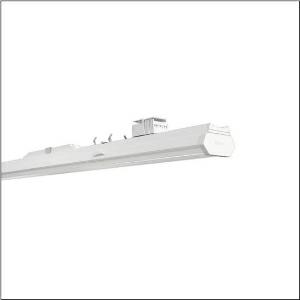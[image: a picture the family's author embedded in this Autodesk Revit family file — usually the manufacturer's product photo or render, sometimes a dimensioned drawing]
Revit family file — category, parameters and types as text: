
# Revit family: licross_r__21_protected_mo_52tp12mn4a5g_3eb5
name_source: partatom
category: Lighting Fixtures
units: mm (PartAtom-declared; Revit-internal decimal feet)

## family parameters
Cut with Voids When Loaded = No
Host = Face
Light Source = No
Part Type = Normal
Room Calculation Point = No
Round Connector Dimension = Use Diameter
Shared = No

## types (1)
- --- (1 x LED, 10750 lm, 60.5 W, 4000K)
    Apparent Load = 61 VA
    CIE Flux Codes = 73 92 98 99 100
    Color Rendering = 80
    Color Temperature = 4000K
    Default Elevation = 1800 mm
    Description = Licross® 21 Protected MO, luminaire insert, of sheet steel, galvanised, coil coated, white, length: 1.500mm, width: 90mm, height: 101mm, LED rated luminous flux: 10.750lm, light colour: 840, control gear: ON/OFF Multilumen, with plug, 3-pole, with phase selection, mains connection: 220..240V, AC, 50/60Hz, rated input power: 61W, halogen-free wiring, primary light control with lens, of plastic, primary optical cover: cover, of PMMA, light emission: direct distribution, primary light characteristic: symmetric, protection rating (complete): IP64, insulation class (complete): insulation class I (protective earthing), certification: CE, ENEC, VDE, UKCA, protection symbol: D if used in an environment with conductive dust loads with corresponding accessories, impact resistance: IK06, permissible ambient temperature for indoor applications: -35..+45°C, corresponds to IFS (International Featured Standards) requirements for safety and quality in the food industry, reducing of maximum allowable ambient temperature of 5°C with ceiling mounting, LABS conformity tested according to VDMA 24364:2018-05, packaging unit: 1 piece
    Height = 92 mm
    Lamp = 1 x LED
    Lamp Light Flux = 10750 lm
    Lamp Power = 60.5 W
    Lamp count = 1
    Length = 1500 mm
    Luminous efficacy = 178 lm/W
    Manufacturer = Siteco
    ModVariant = No
    Model = 52TP12MN4A5G
    Mounting Place = Ceiling
    Mounting Type = Pendant
    Number of Poles = 1
    OnlyDefault = Yes
    Power Factor = 1
    Product Name = Licross® 21 Protected MO
    Product group = luminaire insert
    ProductGroupID = 902
    Protection Class = Protection class I
    Protection Degree = IP 64
    RLX_Detail_Level = 1
    RLX_Emergency_Light_Flux = 0 lm
    RLX_Emergency_Type = 0
    RLX_Emergency_Type_DB = No
    RlxData = <blob elided: 22049 chars, md5=05270d38>
    Socket = socket
    Standby Power = 0 W
    System Light Flux = 10750 lm
    System Power = 61 W
    Type Comments = factory setting: luminous flux: 100 % | (A | C | E) | 140 mA
    Type Image = l_1256148.jpg
    URL = http://relux.com
    VarID = @adj_109126
    Voltage = 0 V
    Weight = 0.00 kg
    Width = 88 mm

## geometry (parser evidence)
native form markers: Blend x4, Sweep x12
no freeform markers — native parametric forms only
